# Revit family: Haworth_Typical_Parametric_Compose_GalleryPanels_L_1Pack
name_source: partatom
category: Furniture Systems
units: mm (PartAtom-declared; Revit-internal decimal feet)

## family parameters
Always vertical = Yes
Cut with Voids When Loaded = No
OmniClass Number = 23.40.70.14.64.21
OmniClass Title = Systems Furniture
Part Type = Normal
Room Calculation Point = No
Round Connector Dimension = Use Diameter
Shared = No
Work Plane-Based = No

## types (2) — shared parameters
Actual Off Spine Height = 42"
Actual Off Spine Length = 72"
Actual Off Spine Length Half = 36"
Actual Off Spine Worksurface Depth = 30"
Actual Spine Height = 42"
Actual Spine Worksurface Depth = 24"
Assembly Code = E2020200
Box Box File = Yes
Classic Pull = No
Corner Length = 24"
Crescent Pull = No
Description = Haworth_Typical_Parametric_Compose_GalleryPanels_2Pack
Enclosure Panels = Yes
End Panel Finish = Haworth _ Laminate _ Undecided _ Panel
File Cabinet Finish = Haworth _ Paint _ Undecided _ Pedestal
File Depth = 29"
File Drawer Finish = Haworth _ Paint _ Undecided _ Pedestal
File Pull Finish = Haworth _ Paint _ Undecided _ Pedestal
Glass Finish = Haworth _ Glass _ Undecided
Hardware Finish = Haworth _ Paint _ Undecided _ Panel
J Pull = Yes
Lateral File = Yes
Linear Pull = No
Manufacturer = Haworth
Max Height = 74"
Max Length = 96"
Max Worksurface Depth = 30"
Maximum Length = 96 in.
Min Height = 34"
Min Length = 60"
Min Worksurface Depth = 18"
Minimum Length = 60 in.
Model = Haworth_Typical_Parametric_Compose_GalleryPanels_2Pack
Multiple Panel Tiles = No
Off Spine Extra Gallery Panel Length = 33"
Off Spine Height = 42"
Off Spine Length = 72"
Off Spine Straight Surface Length = 48"
Off Spine Tile Count = 1
Off Spine Worksurface Depth = 30"
Panel High Tile Finish = Haworth _ Fabric _ Undecided _ Panel
Panel Low Tile Finish = Haworth _ Fabric _ Undecided _ Panel
Radius Pull = No
Revision = 1
Seat Arm Cap Finish = Haworth _ Polymer _ Undecided
Seat Back Upholstery Finish = Haworth _ Fabric _ Undecided _ Seating _ Task Back
Seat Cushion Finish = Haworth _ Fabric _ Undecided _ Seating _ Task Seat
Seat Shell Finish = Haworth _ Paint _ Undecided _ Seating
Seat Support Finish = Haworth _ Polymer _ Undecided
Shared Panels = Yes
Single Panel Tile = Yes
Size = Verify Final Dim. w/ Haworth
Spine End Cap = No
Spine Height = 42"
Spine Tile Count = 1
Spine Worksurface Depth = 24"
Standard Panel Heights = 34, 42, 50, 58, 66, 74 in.
Sustainability Info = www.haworth.com/en-us/About-Us/Sustainability/Pages/Vision.aspx
Task Chair = Yes
URL = http://haworth.com
URL - Product = http://haworth.com
Wardrobe Height = 40 1/2"
Worksurface Edge Finish = Haworth _ Laminate _ Undecided _ Tables
Worksurface Finish = Haworth _ Laminate _ Undecided _ Tables

## per-type parameters (varying)
| type | Actual Spine Length | Actual Spine Length Half | Max Length Wing | Spine End Panel Length | Spine Length |
| 96w 72d - 42h, With Lat, With BBF, With Chair, No Multi Panel Tiles, With Enclosure Panels, With Shared Panels | 96" | 48" | 60" | 72" | 96" |
| 72w 72d - 42h, With Lat, With BBF, With Chair, No Multi Panel Tiles, With Enclosure Panels, With Shared Panels | 72" | 36" | 36" | 48" | 72" |

## geometry (parser evidence)
native form markers: Sweep x55
no freeform markers — native parametric forms only
